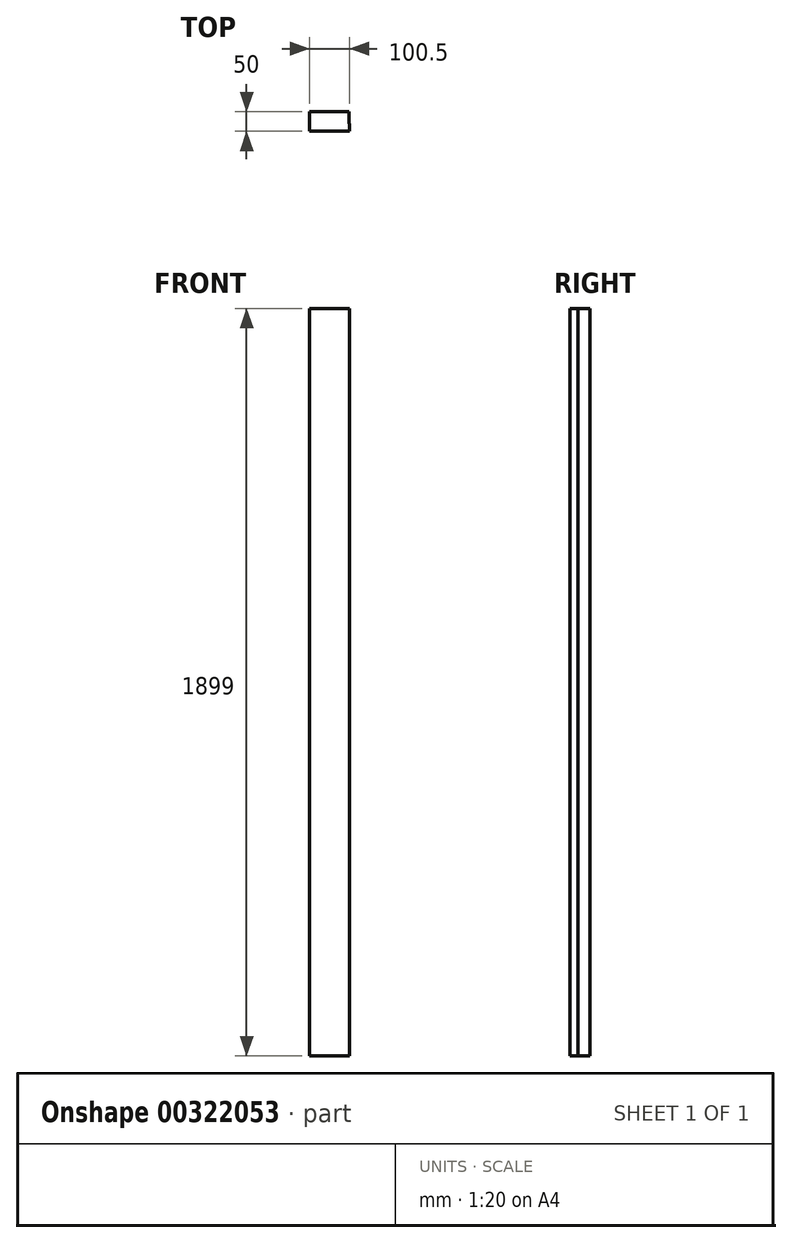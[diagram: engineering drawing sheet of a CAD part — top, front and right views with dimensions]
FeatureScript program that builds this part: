
annotation { "Feature Type Name" : "Feature", "Feature Type Description" : "" }
export const myFeature = defineFeature(function(context is Context, id is Id, definition is map)
    precondition{}
    {
        {
            var Q0;
            Q0=qCreatedBy(makeId("Top.planeOp"),FACE);
            var sketch = newSketch(context, id + "F0", { "sketchPlane" : qUnion([Q0])});
            skLineSegment(sketch, "E0.bottom", {"start": v(50, -25) * mm, "end": v(-50, -25) * mm});
            skLineSegment(sketch, "E0.top", {"start": v(50, 25) * mm, "end": v(-50, 25) * mm});
            skLineSegment(sketch, "E0.left", {"start": v(50, -25) * mm, "end": v(50, 25) * mm});
            skLineSegment(sketch, "E0.right", {"start": v(-50, -25) * mm, "end": v(-50, 25) * mm});
            skPoint(sketch, "E0.middle", {"position": v(0, 0) * mm});
            skSolve(sketch);
        }
        {
            var Q0;
            Q0=makeQuery(id+"F0.imprint","IMPRINT",FACE,{"disambiguationData":[TD([[makeQuery(id+"F0.imprint","IMPRINT",EDGE,{"derivedFrom":sQuery(id+"F0.wireOp",EDGE,"E0.bottom")}),-1.0]])]});
            extrude(context, id + "F1", {"entities" : qUnion([Q0]), "depth" : 1899 * mm});
        }
        {
            var Q0;
            Q0=makeQuery(id+"F1.opExtrude","SWEPT_FACE",FACE,{"disambiguationData":[OSD([sQuery(id+"F0.wireOp",EDGE,"E0.left")])]});
            var sketch = newSketch(context, id + "F2", { "sketchPlane" : qUnion([Q0])});
            skLineSegment(sketch, "E1.0", {"start": v(-5, 1899) * mm, "end": v(-5, 0) * mm});
            skLineSegment(sketch, "E2.0", {"start": v(-30, -5) * mm, "end": v(30, -5) * mm});
            skLineSegment(sketch, "E2.1", {"start": v(-30, 1904) * mm, "end": v(-30, -5) * mm});
            skLineSegment(sketch, "E2.2", {"start": v(30, 1904) * mm, "end": v(-30, 1904) * mm});
            skLineSegment(sketch, "E2.3", {"start": v(30, -5) * mm, "end": v(30, 1904) * mm});
            skSolve(sketch);
        }
        {
            var Q0;
            {var subQ0=sQuery(id+"F2.wireOp",EDGE,"E1.0");Q0=makeQuery(id+"F2.imprint","IMPRINT",FACE,{"disambiguationData":[TD([[makeQuery(id+"F2.imprint","IMPRINT",EDGE,{"derivedFrom":subQ0}),-1.0]])]});}
            extrude(context, id + "F3", {"entities" : qUnion([Q0]), "operationType" : NewBodyOperationType.ADD, "depth" : .5 * mm});
        }
    });
